# Revit family: ALRW
name_source: partatom
category: Lighting Fixtures
units: mm (PartAtom-declared; Revit-internal decimal feet)

## family parameters
Always vertical = Yes
Cut with Voids When Loaded = No
Host = Ceiling
Light Source = Yes
Maintain Annotation Orientation = No
OmniClass Number = 23.80.70.11.14.17
OmniClass Title = Direct/Indirect
Part Type = Normal
Room Calculation Point = No
Round Connector Dimension = Use Diameter
Shared = No

## types (8) — shared parameters
Assembly Code = D5020200
Color Filter = 16777215
Default Elevation = 0' - 0"
Description = LED- Premium-Grade Suspended Linear Luminaire
Dimming Lamp Color Temperature Shift = <None>
Housing Finish = Metal - Viscor - White
Lamp = LED
Lens Finish Bottom = Acrylic - Viscor - Frosted
Lens Finish Top = Acrylic - Viscor - Clear
Manufacturer = VISIONEERING by VISCOR
Model = ALRW
Tilt Angle = 180.00°
URL = https://viscor.com
Voltage = 120 V
Width = 0' - 7 5/8"

## per-type parameters (varying)
| type | Apparent Load | Emit from Line Length | Lamp Wattage | Length | Photometric Web File |
| ALRW48-LED840K05LFUNV-LD64 | 14 VA | 4' - 0" | 14 VA | 4' - 0" | ALRW48-LED840K05LFUNV-LD64.ies |
| ALRW96-LED840K05LFUNV-LD64 | 29 VA | 8' - 0" | 29 VA | 8' - 0" | ALRW96-LED840K05LFUNV-LD64.ies |
| ALRW48-LED840K10LFUNV-LD64 | 28 VA | 4' - 0" | 28 VA | 4' - 0" | ALRW48-LED840K10LFUNV-LD64.ies |
| ALRW48-LED840K15LFUNV-LD64 | 42 VA | 4' - 0" | 42 VA | 4' - 0" | ALRW48-LED840K15LFUNV-LD64.ies |
| ALRW48-LED840K20LFUNV-LD64 | 58 VA | 4' - 0" | 58 VA | 4' - 0" | ALRW48-LED840K20LFUNV-LD64.ies |
| ALRW96-LED840K10LFUNV-LD64 | 55 VA | 8' - 0" | 55 VA | 8' - 0" | ALRW96-LED840K10LFUNV-LD64.ies |
| ALRW96-LED840K15LFUNV-LD64 | 84 VA | 8' - 0" | 84 VA | 8' - 0" | ALRW96-LED840K15LFUNV-LD64.ies |
| ALRW96-LED840K20LFUNV-LD64 | 116 VA | 8' - 0" | 116 VA | 8' - 0" | ALRW96-LED840K20LFUNV-LD64.ies |

## geometry (parser evidence)
native form markers: Sweep x3
no freeform markers — native parametric forms only
